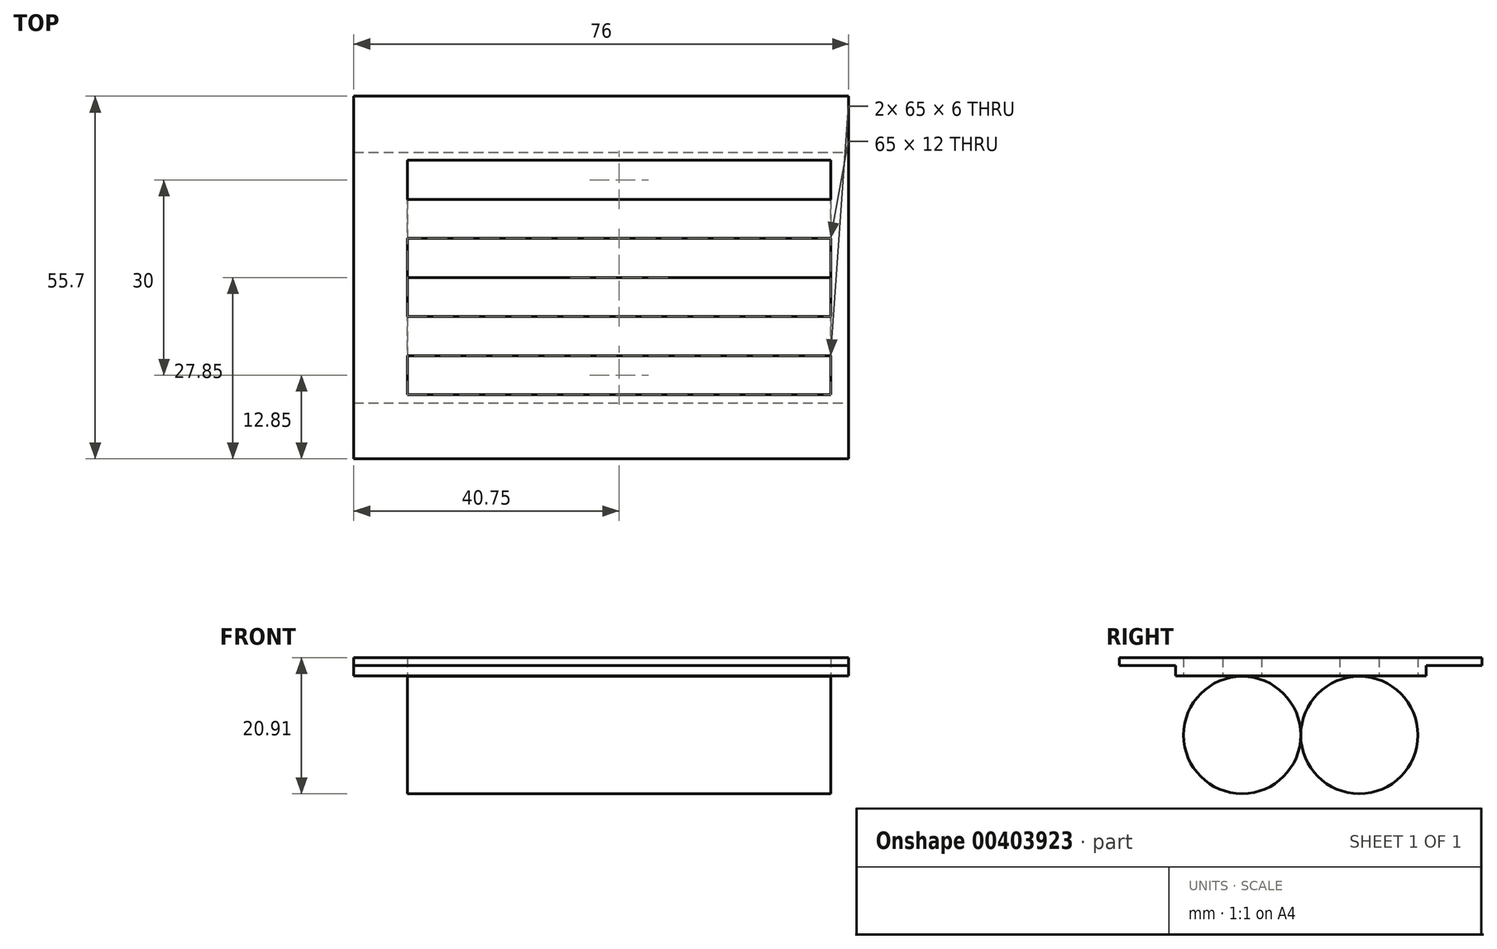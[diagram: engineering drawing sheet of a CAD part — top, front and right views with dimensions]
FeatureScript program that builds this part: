
annotation { "Feature Type Name" : "Feature", "Feature Type Description" : "" }
export const myFeature = defineFeature(function(context is Context, id is Id, definition is map)
    precondition{}
    {
        {
            var Q0;
            Q0=qCreatedBy(makeId("Right.planeOp"),FACE);
            var sketch = newSketch(context, id + "F0", { "sketchPlane" : qUnion([Q0])});
            skCircle(sketch, "E0", {"center": v(9, -9.1) * mm, "radius": 9 * mm});
            skCircle(sketch, "E1", {"center": v(-9, -9.1) * mm, "radius": 9 * mm});
            skLineSegment(sketch, "E2", {"start": v(0, 0) * mm, "end": v(0, -28.78) * mm, "construction": true});
            skSolve(sketch);
        }
        {
            var Q0;
            Q0 = qSketchRegion(id + "F0", true);
            extrude(context, id + "F1", {"entities" : qUnion([Q0]), "endBound" : BoundingType.SYMMETRIC, "depth" : 65 * mm});
        }
        {
            var Q0;
            Q0=qCreatedBy(makeId("Top.planeOp"),FACE);
            var sketch = newSketch(context, id + "F2", { "sketchPlane" : qUnion([Q0])});
            skLineSegment(sketch, "E3.bottom", {"start": v(-40.75, 19.25) * mm, "end": v(35.25, 19.25) * mm});
            skLineSegment(sketch, "E3.top", {"start": v(-40.75, -19.25) * mm, "end": v(35.25, -19.25) * mm});
            skLineSegment(sketch, "E3.left", {"start": v(-40.75, 19.25) * mm, "end": v(-40.75, -19.25) * mm});
            skLineSegment(sketch, "E3.right", {"start": v(35.25, 19.25) * mm, "end": v(35.25, -19.25) * mm});
            skLineSegment(sketch, "E4", {"start": v(35.25, 0) * mm, "end": v(-7.2, 0) * mm, "construction": true});
            skLineSegment(sketch, "E5.0", {"start": v(-32.5, 18) * mm, "end": v(-32.5, 0) * mm});
            skLineSegment(sketch, "E6.0", {"start": v(-32.5, 0) * mm, "end": v(-32.5, -18) * mm});
            skLineSegment(sketch, "E7", {"start": v(32.5, -18) * mm, "end": v(-32.5, -18) * mm});
            skLineSegment(sketch, "E8.0", {"start": v(32.5, 0) * mm, "end": v(32.5, -18) * mm});
            skLineSegment(sketch, "E9.0", {"start": v(32.5, 18) * mm, "end": v(32.5, 0) * mm});
            skLineSegment(sketch, "E10", {"start": v(-32.5, 18) * mm, "end": v(32.5, 18) * mm});
            skLineSegment(sketch, "E11", {"start": v(-32.5, -9) * mm, "end": v(32.5, -9) * mm, "construction": true});
            skLineSegment(sketch, "E12", {"start": v(-32.5, 9) * mm, "end": v(32.5, 9) * mm, "construction": true});
            skLineSegment(sketch, "E13.0", {"start": v(-32.5, 12) * mm, "end": v(32.5, 12) * mm});
            skLineSegment(sketch, "E14.0", {"start": v(-32.5, 6) * mm, "end": v(32.5, 6) * mm});
            skLineSegment(sketch, "E15.0", {"start": v(-32.5, -6) * mm, "end": v(32.5, -6) * mm});
            skLineSegment(sketch, "E16.0", {"start": v(-32.5, -12) * mm, "end": v(32.5, -12) * mm});
            skSolve(sketch);
        }
        {
            var Q0;
            Q0 = qSketchRegion(id + "F2", true);
            var Q1;
            {var subQ0=sQuery(id+"F2.wireOp",EDGE,"E15.0");Q1=makeQuery(id+"F2.imprint","IMPRINT",FACE,{"disambiguationData":[TD([[makeQuery(id+"F2.imprint","IMPRINT",EDGE,{"derivedFrom":subQ0}),-1.0]])]});}
            var Q2;
            {var subQ0=sQuery(id+"F2.wireOp",EDGE,"E13.0");Q2=makeQuery(id+"F2.imprint","IMPRINT",FACE,{"disambiguationData":[TD([[makeQuery(id+"F2.imprint","IMPRINT",EDGE,{"derivedFrom":subQ0}),-1.0]])]});}
            extrude(context, id + "F3", {"entities" : qUnion([Q0, Q1, Q2]), "depth" : 2.8 * mm});
        }
        {
            var Q0;
            Q0=makeQuery(id+"F3.opExtrude","CAP_FACE",FACE,{"disambiguationData":[OSD([sQuery(id+"F2.wireOp",EDGE,"E3.bottom"),sQuery(id+"F2.wireOp",EDGE,"E3.top"),sQuery(id+"F2.wireOp",EDGE,"E3.left"),sQuery(id+"F2.wireOp",EDGE,"E3.right"),sQuery(id+"F2.wireOp",EDGE,"E5.0"),sQuery(id+"F2.wireOp",EDGE,"E6.0"),sQuery(id+"F2.wireOp",EDGE,"E7"),sQuery(id+"F2.wireOp",EDGE,"E8.0"),sQuery(id+"F2.wireOp",EDGE,"E9.0"),sQuery(id+"F2.wireOp",EDGE,"E10"),sQuery(id+"F2.wireOp",EDGE,"E13.0"),sQuery(id+"F2.wireOp",EDGE,"E14.0"),sQuery(id+"F2.wireOp",EDGE,"E15.0"),sQuery(id+"F2.wireOp",EDGE,"E16.0")])],"isStart":false});
            var sketch = newSketch(context, id + "F4", { "sketchPlane" : qUnion([Q0])});
            skLineSegment(sketch, "E17.bottom", {"start": v(-40.75, 27.85) * mm, "end": v(35.25, 27.85) * mm});
            skLineSegment(sketch, "E17.top", {"start": v(-40.75, -27.85) * mm, "end": v(35.25, -27.85) * mm});
            skLineSegment(sketch, "E17.left", {"start": v(-40.75, 27.85) * mm, "end": v(-40.75, -27.85) * mm});
            skLineSegment(sketch, "E17.right", {"start": v(35.25, 27.85) * mm, "end": v(35.25, -27.85) * mm});
            skLineSegment(sketch, "E18", {"start": v(-40.75, 0) * mm, "end": v(5.98, 0) * mm, "construction": true});
            skSolve(sketch);
        }
        {
            var Q0;
            {var subQ0=sQuery(id+"F4.wireOp",EDGE,"E17.bottom");Q0=makeQuery(id+"F4.imprint","IMPRINT",FACE,{"disambiguationData":[TD([[makeQuery(id+"F4.imprint","IMPRINT",EDGE,{"derivedFrom":subQ0}),-1.0]])]});}
            var Q1;
            {var subQ0=sQuery(id+"F4.wireOp",EDGE,"E17.top");Q1=makeQuery(id+"F4.imprint","IMPRINT",FACE,{"disambiguationData":[TD([[makeQuery(id+"F4.imprint","IMPRINT",EDGE,{"derivedFrom":subQ0}),1.0]])]});}
            extrude(context, id + "F5", {"entities" : qUnion([Q0, Q1]), "operationType" : NewBodyOperationType.ADD, "oppositeDirection" : true, "depth" : 1.2 * mm});
        }
    });
